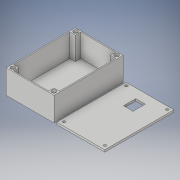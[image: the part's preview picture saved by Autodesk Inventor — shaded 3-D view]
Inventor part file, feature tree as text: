
AUTODESK INVENTOR PART (.ipt)
format: ipt  version: 2019 (Build 230136000, 136)  size: 324,608 bytes
history: native  units: mm
features: extrude x6, sketch x6, pattern_linear x3, shell x1
ambient origin geometry x8: Origin, YZ Plane, XZ Plane, XY Plane, X Axis, Y Axis, Z Axis, Center Point
bodies: Solid1 (feature_tree)
feature tree (16):
  extrude  "Extrusion1"  Depth=130.0mm
  shell  "Shell1"  Thickness=45.0mm
  extrude  "Extrusion2"  Depth=10.0mm
  pattern_linear  "Rectangular Pattern1"  Count1=2 Spacing1=116.0mm
  extrude  "Extrusion3"  Depth=76.0mm
  pattern_linear  "Rectangular Pattern2"  Count1=2 Spacing1=118.0mm
  extrude  "Extrusion7"  Depth=4.0mm
  extrude  "Extrusion8"  Depth=90.0mm
  pattern_linear  "Rectangular Pattern4"  Count1=13  [1 undecoded]
  extrude  "Extrusion9"  Depth=4.0mm TaperAngle=0.0deg
  sketch  "Sketch1"  dims[d0=90.0mm d1=130.0mm d2=45.0mm d3=0.0mm]
  sketch  "Sketch2"  dims[d4=2.0mm d5=10.0mm]
  sketch  "Sketch3"  dims[d6=10.0mm]
  sketch  "Sketch7"  dims[d7=43.0mm d8=0.0mm d9=20.0mm d11=116.0mm]
  sketch  "Sketch8"  dims[d12=20.0mm d14=76.0mm d15=8.0mm]
  sketch  "Sketch9"  dims[d16=4.0mm d17=0.0mm d18=20.0mm d20=118.0mm d21=20.0mm d23=77.0mm d41=90.0mm d42=130.0mm d43=4.0mm d44=0.0mm d45=4.0mm d46=0.0mm d47=20.0mm d49=77.0mm d50=20.0mm d52=117.0mm d53=9.0mm d54=23.0mm d55=18.0mm d56=4.0mm d57=0.0mm]
note: 1 required parameter value undecoded (feature->parameter linkage not recoverable at this tier; creation-order binding heuristic only, values carry confidence <= 0.55)
